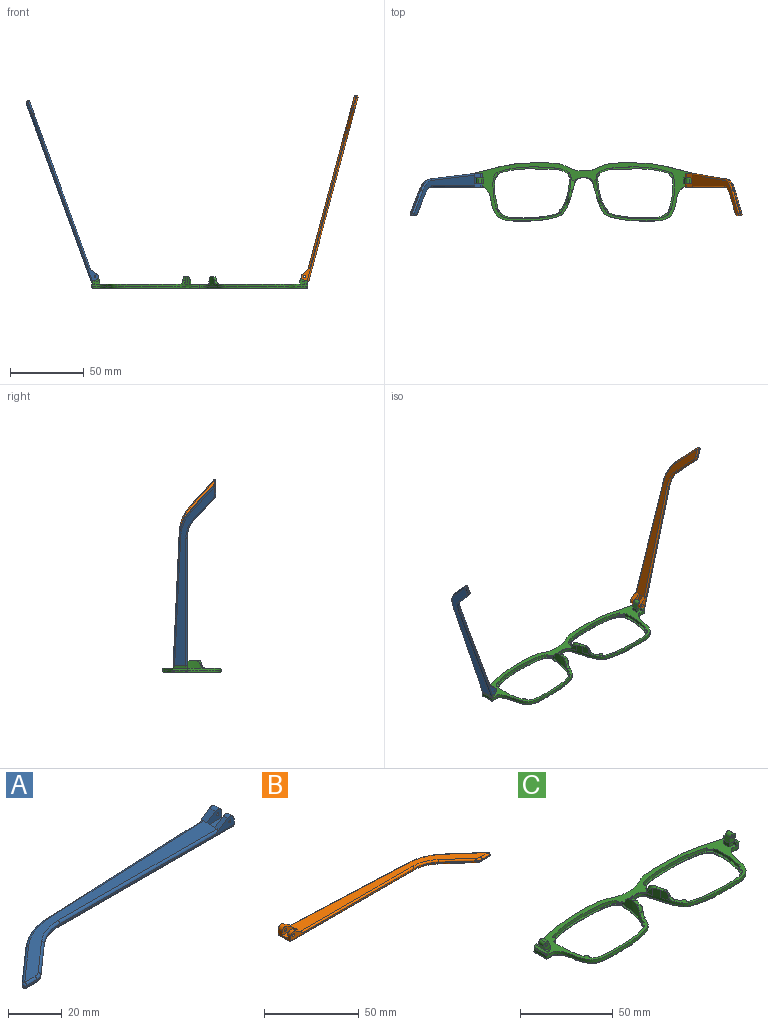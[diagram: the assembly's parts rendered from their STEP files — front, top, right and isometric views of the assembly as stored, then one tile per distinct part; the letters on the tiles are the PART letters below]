
ASSEMBLY  parts=3 mates=1
PART A: 43 faces, bbox 130.2x29.5x5.9 mm
  f0: plane 9.62x3.72mm, normal (1,0,0), area 24.7mm2, adj f1,f3,f4,f5,f10,f16,f18,f28
  f1: cylinder r=2.2mm len=3.45mm, axis (0,-1,0), area 11mm2, adj f0,f2,f4,f37
  f2: plane 6.01x3.91mm, normal (-0.55,0,0.84), area 12.7mm2, adj f1,f4,f9,f19,f37
  f3: plane 2.26x0.1mm, normal (0,0,1), area 0.1mm2, adj f0,f5,f18
  f4: plane 92.1x4.9mm, normal (0,-1,0), area 79.9mm2, adj f0,f1,f2,f14,f19,f36,f42
  f5: plane 93.42x4.13mm, normal (-0.04,1,0), area 64.8mm2, adj f0,f3,f11,f15,f17,f27,f28
  f6: plane 17.82x15.72mm, normal (-0.66,0.75,0), area 14.3mm2, adj f11,f12,f25,f30
  f7: plane 5.46x0.6mm, normal (0,-1,0), area 3.3mm2, adj f12,f13,f23,f32
  f8: plane 14.99x13.23mm, normal (0.66,-0.75,0), area 12mm2, adj f13,f14,f21,f34
  f9: plane 121.18x26.73mm, normal (0,0,1), area 627.7mm2, adj f2,f17,f19,f20,f21,f22,f23,f25
  f10: plane 129.1x27.08mm, normal (0,0,-1), area 686.5mm2, adj f0,f28,f29,f30,f32,f33,f34,f35
  f11: cylinder r=30mm len=18.52mm, axis (0,0,-1), area 12.2mm2, adj f5,f6,f26,f29
  f12: cylinder r=1mm len=1.75mm, axis (0,0,-1), area 1.5mm2, adj f6,f7,f24,f31
  f13: cylinder r=5mm len=3.31mm, axis (0,0,-1), area 2.2mm2, adj f7,f8,f22,f33
  f14: cylinder r=20mm len=13.23mm, axis (0,0,1), area 8.7mm2, adj f4,f8,f20,f35
  f15: plane 5.66x0.25mm, normal (0,0,-1), area 0.7mm2, adj f5,f17,f18
  f16: cylinder r=2.2mm len=3.45mm, axis (0,-1,0), area 14.8mm2, adj f0,f17,f18,f38
  f17: plane 6.01x3.91mm, normal (-0.55,0,0.84), area 16.9mm2, adj f5,f9,f15,f16,f18,f27,f38
  f18: plane 7.92x3.3mm, normal (0,1,0), area 15.9mm2, adj f0,f3,f15,f16,f17,f41
  f19: cylinder r=1mm len=84.18mm, axis (-1,0,0), area 131.4mm2, adj f2,f4,f9,f20
  f20: torus R=21mm, axis (0,0,1), area 23.1mm2, adj f9,f14,f19,f21
  f21: cylinder r=1mm len=15.65mm, axis (-0.75,-0.66,0), area 31.4mm2, adj f8,f9,f20,f22
  f22: torus R=4mm, axis (0,0,1), area 5.3mm2, adj f9,f13,f21,f23
  f23: cylinder r=1mm len=5.46mm, axis (-1,0,0), area 8.6mm2, adj f7,f9,f22,f24
  f24: sphere r=1mm, area 2.4mm2, adj f12,f23,f25
  f25: cylinder r=1mm len=18.48mm, axis (0.75,0.66,0), area 37.3mm2, adj f6,f9,f24,f26
  f26: torus R=29mm, axis (0,0,1), area 31.6mm2, adj f9,f11,f25,f27
  f27: cylinder r=1mm len=85.5mm, axis (1,0.04,0), area 133.5mm2, adj f5,f9,f17,f26
  f28: cylinder r=1mm len=93.46mm, axis (-1,-0.04,0), area 146.9mm2, adj f0,f5,f10,f29
  f29: torus R=29mm, axis (0,0,1), area 31.6mm2, adj f10,f11,f28,f30
  f30: cylinder r=1mm len=18.48mm, axis (-0.75,-0.66,0), area 37.3mm2, adj f6,f10,f29,f31
  f31: sphere r=1mm, area 2.4mm2, adj f12,f30,f32
  f32: cylinder r=1mm len=5.46mm, axis (1,0,0), area 8.6mm2, adj f7,f10,f31,f33
  f33: torus R=4mm, axis (0,0,1), area 5.3mm2, adj f10,f13,f32,f34
  f34: cylinder r=1mm len=15.65mm, axis (0.75,0.66,0), area 31.4mm2, adj f8,f10,f33,f35
  f35: torus R=21mm, axis (0,0,1), area 23.1mm2, adj f10,f14,f34,f36
  f36: cylinder r=1mm len=92.1mm, axis (1,0,0), area 144.7mm2, adj f0,f4,f10,f35
  f37: plane 7.92x4.7mm, normal (0,1,0), area 27mm2, adj f0,f1,f2,f39,f40,f42
  f38: plane 7.92x4.7mm, normal (0,-1,0), area 27mm2, adj f0,f16,f17,f39,f40,f41
  f39: plane 7.92x4.1mm, normal (0,0,1), area 32.5mm2, adj f0,f37,f38,f40
  f40: plane 4.1x1.4mm, normal (1,0,0), area 5.7mm2, adj f9,f37,f38,f39
  f41: cylinder r=0.5mm len=3.1mm, axis (0,-1,0), area 9.7mm2, adj f18,f38
  f42: cylinder r=0.5mm len=2.3mm, axis (0,-1,0), area 7.2mm2, adj f4,f37
PART B: 43 faces, bbox 130.2x29.5x5.9 mm
  f0: plane 9.62x3.72mm, normal (-1,0,0), area 24.7mm2, adj f1,f3,f4,f5,f10,f16,f18,f28
  f1: cylinder r=2.2mm len=3.45mm, axis (0,-1,0), area 11mm2, adj f0,f2,f4,f37
  f2: plane 6.01x3.91mm, normal (0.55,0,0.84), area 12.7mm2, adj f1,f4,f9,f19,f37
  f3: plane 2.26x0.1mm, normal (0,0,1), area 0.1mm2, adj f0,f5,f18
  f4: plane 92.1x4.9mm, normal (0,-1,0), area 78.2mm2, adj f0,f1,f2,f14,f19,f36,f42
  f5: plane 93.42x4.13mm, normal (0.04,1,0), area 64.8mm2, adj f0,f3,f11,f15,f17,f27,f28
  f6: plane 17.82x15.72mm, normal (0.66,0.75,0), area 14.3mm2, adj f11,f12,f25,f30
  f7: plane 5.46x0.6mm, normal (0,-1,0), area 3.3mm2, adj f12,f13,f23,f32
  f8: plane 14.99x13.23mm, normal (-0.66,-0.75,0), area 12mm2, adj f13,f14,f21,f34
  f9: plane 121.18x26.73mm, normal (0,0,1), area 627.7mm2, adj f2,f17,f19,f20,f21,f22,f23,f25
  f10: plane 129.1x27.08mm, normal (0,0,-1), area 686.5mm2, adj f0,f28,f29,f30,f32,f33,f34,f35
  f11: cylinder r=30mm len=18.52mm, axis (0,0,-1), area 12.2mm2, adj f5,f6,f26,f29
  f12: cylinder r=1mm len=1.75mm, axis (0,0,-1), area 1.5mm2, adj f6,f7,f24,f31
  f13: cylinder r=5mm len=3.31mm, axis (0,0,-1), area 2.2mm2, adj f7,f8,f22,f33
  f14: cylinder r=20mm len=13.23mm, axis (0,0,1), area 8.7mm2, adj f4,f8,f20,f35
  f15: plane 5.66x0.25mm, normal (0,0,-1), area 0.7mm2, adj f5,f17,f18
  f16: cylinder r=2.2mm len=3.45mm, axis (0,-1,0), area 14.8mm2, adj f0,f17,f18,f38
  f17: plane 6.01x3.91mm, normal (0.55,0,0.84), area 16.9mm2, adj f5,f9,f15,f16,f18,f27,f38
  f18: plane 7.92x3.3mm, normal (0,1,0), area 14.3mm2, adj f0,f3,f15,f16,f17,f41
  f19: cylinder r=1mm len=84.18mm, axis (1,0,0), area 131.4mm2, adj f2,f4,f9,f20
  f20: torus R=21mm, axis (0,0,1), area 23.1mm2, adj f9,f14,f19,f21
  f21: cylinder r=1mm len=15.65mm, axis (0.75,-0.66,0), area 31.4mm2, adj f8,f9,f20,f22
  f22: torus R=4mm, axis (0,0,1), area 5.3mm2, adj f9,f13,f21,f23
  f23: cylinder r=1mm len=5.46mm, axis (1,0,0), area 8.6mm2, adj f7,f9,f22,f24
  f24: sphere r=1mm, area 2.4mm2, adj f12,f23,f25
  f25: cylinder r=1mm len=18.48mm, axis (-0.75,0.66,0), area 37.3mm2, adj f6,f9,f24,f26
  f26: torus R=29mm, axis (0,0,1), area 31.6mm2, adj f9,f11,f25,f27
  f27: cylinder r=1mm len=85.5mm, axis (-1,0.04,0), area 133.5mm2, adj f5,f9,f17,f26
  f28: cylinder r=1mm len=93.46mm, axis (1,-0.04,0), area 146.9mm2, adj f0,f5,f10,f29
  f29: torus R=29mm, axis (0,0,1), area 31.6mm2, adj f10,f11,f28,f30
  f30: cylinder r=1mm len=18.48mm, axis (0.75,-0.66,0), area 37.3mm2, adj f6,f10,f29,f31
  f31: sphere r=1mm, area 2.4mm2, adj f12,f30,f32
  f32: cylinder r=1mm len=5.46mm, axis (-1,0,0), area 8.6mm2, adj f7,f10,f31,f33
  f33: torus R=4mm, axis (0,0,1), area 5.3mm2, adj f10,f13,f32,f34
  f34: cylinder r=1mm len=15.65mm, axis (-0.75,0.66,0), area 31.4mm2, adj f8,f10,f33,f35
  f35: torus R=21mm, axis (0,0,1), area 23.1mm2, adj f10,f14,f34,f36
  f36: cylinder r=1mm len=92.1mm, axis (-1,0,0), area 144.7mm2, adj f0,f4,f10,f35
  f37: plane 7.92x4.7mm, normal (0,1,0), area 25.4mm2, adj f0,f1,f2,f39,f40,f42
  f38: plane 7.92x4.7mm, normal (0,-1,0), area 25.4mm2, adj f0,f16,f17,f39,f40,f41
  f39: plane 7.92x4.1mm, normal (0,0,1), area 32.5mm2, adj f0,f37,f38,f40
  f40: plane 4.1x1.4mm, normal (-1,0,0), area 5.7mm2, adj f9,f37,f38,f39
  f41: cylinder r=0.88mm len=3.1mm, axis (0,-1,0), area 17mm2, adj f18,f38
  f42: cylinder r=0.88mm len=2.3mm, axis (0,-1,0), area 12.6mm2, adj f4,f37
PART C: 100 faces, bbox 148x40.2x17.8 mm
  f0: plane 147.39x39.85mm, normal (0,0,1), area 920.1mm2, adj f2,f3,f4,f5,f6,f9,f17,f20
  f1: plane 4.47x1.42mm, normal (0,0,1), area 0.1mm2, adj f5,f35
  f2: plane 1.27x0.04mm, normal (0,0,1), area 0mm2, adj f0,f5,f19
  f3: plane 6.97x5.07mm, normal (0,1,0), area 22.7mm2, adj f0,f17,f18,f22,f24,f25,f27,f28
  f4: plane 3.2x2.36mm, normal (0,-1,0), area 5.7mm2, adj f0,f17,f23,f26
  f5: extruded ~73.26x39.54mm, area 285.8mm2, adj f0,f1,f2,f6,f10,f11,f12,f13
  f6: extruded ~35.3x5.43mm, area 72.3mm2, adj f0,f5,f15,f56
  f7: plane 144.78x37.58mm, normal (0,0,-1), area 666.4mm2, adj f10,f12,f14,f15,f16,f59,f61,f63
  f8: plane 53.26x35.52mm, normal (0,0,1), area 153mm2, adj f9,f16
  f9: extruded ~53.07x35.37mm, area 383.8mm2, adj f0,f8,f36,f37,f38,f39,f40,f41
  f10: bspline ~72.84x30.37mm, area 162.4mm2, adj f5,f7,f11,f59
  f11: bspline ~1x1mm, area 0.8mm2, adj f5,f10,f12
  f12: bspline ~9.85x1.31mm, area 12.6mm2, adj f5,f7,f11,f13
  f13: bspline ~1.04x1mm, area 0.8mm2, adj f5,f12,f14
  f14: bspline ~41.9x8.02mm, area 59.9mm2, adj f5,f7,f13,f15
  f15: bspline ~40.28x6.43mm, area 56.8mm2, adj f6,f7,f14,f64
  f16: bspline ~52.92x35.45mm, area 231.7mm2, adj f7,f8
  f17: plane 4x2.36mm, normal (-1,0,0), area 9.5mm2, adj f0,f3,f4,f18
  f18: plane 4x0.02mm, normal (0.34,0,0.94), area 0.1mm2, adj f3,f17,f25
  f19: plane 2.72x2.49mm, normal (0,-1,0), area 3.9mm2, adj f2,f23,f24,f32,f48
  f20: plane 7.66x1.6mm, normal (0.94,0,-0.34), area 13mm2, adj f0,f32,f33,f48
  f21: plane 2.1x1.68mm, normal (0,1,0), area 2.8mm2, adj f0,f22,f24,f33,f48
  f22: plane 3.3x2.1mm, normal (-1,0,0), area 6.9mm2, adj f0,f3,f21,f24
  f23: plane 2.33x2.1mm, normal (-1,0,0), area 4.9mm2, adj f0,f4,f19,f24,f26
  f24: plane 9.64x1.24mm, normal (0,0,1), area 8.2mm2, adj f3,f19,f21,f22,f23,f26,f27,f48
  f25: plane 4x3.31mm, normal (-0.94,0,0.34), area 14.1mm2, adj f3,f18,f26,f29
  f26: plane 5.77x5.06mm, normal (0,-1,0), area 17mm2, adj f4,f23,f24,f25,f27,f28,f29,f30
  f27: plane 4x2.21mm, normal (0.94,0,-0.34), area 9.4mm2, adj f3,f24,f26,f30
  f28: plane 4x0.01mm, normal (0.34,0,0.94), area 0mm2, adj f3,f26,f29,f30
  f29: cylinder r=1.98mm len=4mm, axis (0,1,0), area 12.4mm2, adj f3,f25,f26,f28
  f30: cylinder r=1.98mm len=4mm, axis (0,-1,0), area 12.4mm2, adj f3,f26,f27,f28
  f31: cylinder r=0.88mm len=4mm, axis (0,-1,0), area 22mm2, adj f3,f26
  f32: cone r=1mm half-angle=20deg, axis (0,0,1), area 2.2mm2, adj f0,f19,f20,f48
  f33: cylinder r=1mm len=2.28mm, axis (-0.34,0,-0.94), area 3mm2, adj f0,f20,f21,f48
  f34: extruded ~4.67x3.66mm, area 11.1mm2, adj f5,f37,f50
  f35: extruded ~5x4.44mm, area 22.1mm2, adj f1,f5,f36,f38,f47
  f36: plane 7.44x2.68mm, normal (0,0,1), area 9.9mm2, adj f5,f9,f35,f37,f38
  f37: bspline ~15.47x15.46mm, area 24.4mm2, adj f0,f5,f9,f34,f36,f49
  f38: bspline ~6.53x5.13mm, area 9.5mm2, adj f9,f35,f36,f47
  f39: cylinder r=1.94mm len=3.21mm, axis (0,0,1), area 2.3mm2, adj f0,f9,f40
  f40: plane 3.25x2.06mm, normal (0,0,-1), area 3.9mm2, adj f9,f39
  f41: cylinder r=1.94mm len=3.33mm, axis (0,0,1), area 2.8mm2, adj f0,f9,f42
  f42: plane 3.36x2.87mm, normal (0,0,-1), area 6.1mm2, adj f9,f41
  f43: cylinder r=1.42mm len=2.62mm, axis (0,0,1), area 2.3mm2, adj f0,f9,f44
  f44: plane 2.64x2.34mm, normal (0,0,-1), area 3.7mm2, adj f9,f43
  f45: cylinder r=1.42mm len=2.6mm, axis (0,0,1), area 2.1mm2, adj f0,f9,f46
  f46: plane 2.62x1.92mm, normal (0,0,-1), area 2.8mm2, adj f9,f45
  f47: bspline ~3.71x3.66mm, area 7.7mm2, adj f0,f5,f9,f35,f38
  f48: plane 9.69x1.44mm, normal (0.34,0,0.94), area 13.9mm2, adj f19,f20,f21,f24,f32,f33
  f49: bspline ~7.05x3.31mm, area 3.3mm2, adj f0,f5,f37,f98
  f50: bspline ~5.24x1.76mm, area 0mm2, adj f5,f34
  f51: plane 4.47x1.42mm, normal (0,0,1), area 0.1mm2, adj f55,f84
  f52: plane 1.27x0.04mm, normal (0,0,1), area 0mm2, adj f0,f55,f68
  f53: plane 6.97x5.07mm, normal (0,1,0), area 22.7mm2, adj f0,f66,f67,f71,f73,f74,f76,f77
  f54: plane 3.2x2.36mm, normal (0,-1,0), area 5.7mm2, adj f0,f66,f72,f75
  f55: extruded ~73.26x39.54mm, area 285.8mm2, adj f0,f5,f51,f52,f56,f59,f60,f61
  f56: extruded ~35.3x5.43mm, area 72.3mm2, adj f0,f6,f55,f64
  f57: plane 53.26x35.52mm, normal (0,0,1), area 153mm2, adj f58,f65
  f58: extruded ~53.07x35.37mm, area 383.8mm2, adj f0,f57,f85,f86,f87,f88,f89,f90
  f59: bspline ~72.81x30.37mm, area 162.5mm2, adj f7,f10,f55,f60
  f60: bspline ~1x1mm, area 0.8mm2, adj f55,f59,f61
  f61: bspline ~9.85x1.31mm, area 12.6mm2, adj f7,f55,f60,f62
  f62: bspline ~1.04x1mm, area 0.7mm2, adj f55,f61,f63
  f63: bspline ~41.9x8.02mm, area 59.9mm2, adj f7,f55,f62,f64
  f64: bspline ~40.28x6.43mm, area 56.8mm2, adj f7,f15,f56,f63
  f65: bspline ~52.92x35.45mm, area 231.7mm2, adj f7,f57
  f66: plane 4x2.36mm, normal (1,0,0), area 9.5mm2, adj f0,f53,f54,f67
  f67: plane 4x0.02mm, normal (-0.34,0,0.94), area 0.1mm2, adj f53,f66,f74
  f68: plane 2.72x2.49mm, normal (0,-1,0), area 3.9mm2, adj f52,f72,f73,f81,f97
  f69: plane 7.66x1.6mm, normal (-0.94,0,-0.34), area 13mm2, adj f0,f81,f82,f97
  f70: plane 2.1x1.68mm, normal (0,1,0), area 2.8mm2, adj f0,f71,f73,f82,f97
  f71: plane 3.3x2.1mm, normal (1,0,0), area 6.9mm2, adj f0,f53,f70,f73
  f72: plane 2.33x2.1mm, normal (1,0,0), area 4.9mm2, adj f0,f54,f68,f73,f75
  f73: plane 9.64x1.24mm, normal (0,0,1), area 8.2mm2, adj f53,f68,f70,f71,f72,f75,f76,f97
  f74: plane 4x3.31mm, normal (0.94,0,0.34), area 14.1mm2, adj f53,f67,f75,f78
  f75: plane 5.77x5.06mm, normal (0,-1,0), area 17mm2, adj f54,f72,f73,f74,f76,f77,f78,f79
  f76: plane 4x2.21mm, normal (-0.94,0,-0.34), area 9.4mm2, adj f53,f73,f75,f79
  f77: plane 4x0.01mm, normal (-0.34,0,0.94), area 0mm2, adj f53,f75,f78,f79
  f78: cylinder r=1.98mm len=4mm, axis (0,1,0), area 12.4mm2, adj f53,f74,f75,f77
  f79: cylinder r=1.98mm len=4mm, axis (0,-1,0), area 12.4mm2, adj f53,f75,f76,f77
  f80: cylinder r=0.88mm len=4mm, axis (0,-1,0), area 22mm2, adj f53,f75
  f81: cone r=1mm half-angle=20deg, axis (0,0,1), area 2.2mm2, adj f0,f68,f69,f97
  f82: cylinder r=1mm len=2.28mm, axis (0.34,0,-0.94), area 3mm2, adj f0,f69,f70,f97
  f83: extruded ~4.67x3.66mm, area 11.1mm2, adj f55,f86,f99
  f84: extruded ~5x4.44mm, area 22.1mm2, adj f51,f55,f85,f87,f96
  f85: plane 7.44x2.68mm, normal (0,0,1), area 9.9mm2, adj f55,f58,f84,f86,f87
  f86: bspline ~15.47x15.46mm, area 24.4mm2, adj f0,f55,f58,f83,f85,f98
  f87: bspline ~6.53x5.13mm, area 9.5mm2, adj f58,f84,f85,f96
  f88: cylinder r=1.94mm len=3.21mm, axis (0,0,1), area 2.3mm2, adj f0,f58,f89
  f89: plane 3.25x2.06mm, normal (0,0,-1), area 3.9mm2, adj f58,f88
  f90: cylinder r=1.94mm len=3.33mm, axis (0,0,1), area 2.8mm2, adj f0,f58,f91
  f91: plane 3.36x2.87mm, normal (0,0,-1), area 6.1mm2, adj f58,f90
  f92: cylinder r=1.42mm len=2.62mm, axis (0,0,1), area 2.3mm2, adj f0,f58,f93
  f93: plane 2.64x2.34mm, normal (0,0,-1), area 3.7mm2, adj f58,f92
  f94: cylinder r=1.42mm len=2.6mm, axis (0,0,1), area 2.1mm2, adj f0,f58,f95
  f95: plane 2.62x1.92mm, normal (0,0,-1), area 2.8mm2, adj f58,f94
  f96: bspline ~3.71x3.66mm, area 7.7mm2, adj f0,f55,f58,f84,f87
  f97: plane 9.69x1.44mm, normal (-0.34,0,0.94), area 13.9mm2, adj f68,f69,f70,f73,f81,f82
  f98: bspline ~7.05x3.31mm, area 3.3mm2, adj f0,f49,f55,f86
  f99: bspline ~5.24x1.76mm, area 0mm2, adj f55,f83
PLACE A rot(axis=(0,1,0),70deg) t=(-84.77,-5.75,56)mm
PLACE B rot(axis=(0,-1,0),75deg) t=(68.2,-5.75,-61.61)mm
PLACE C t=(10.15,-1.13,-5.77)mm
MATE revolute B.f41 <-> C.f30  axis (0,-1,0) through (81.2,2.72,1.21)mm
